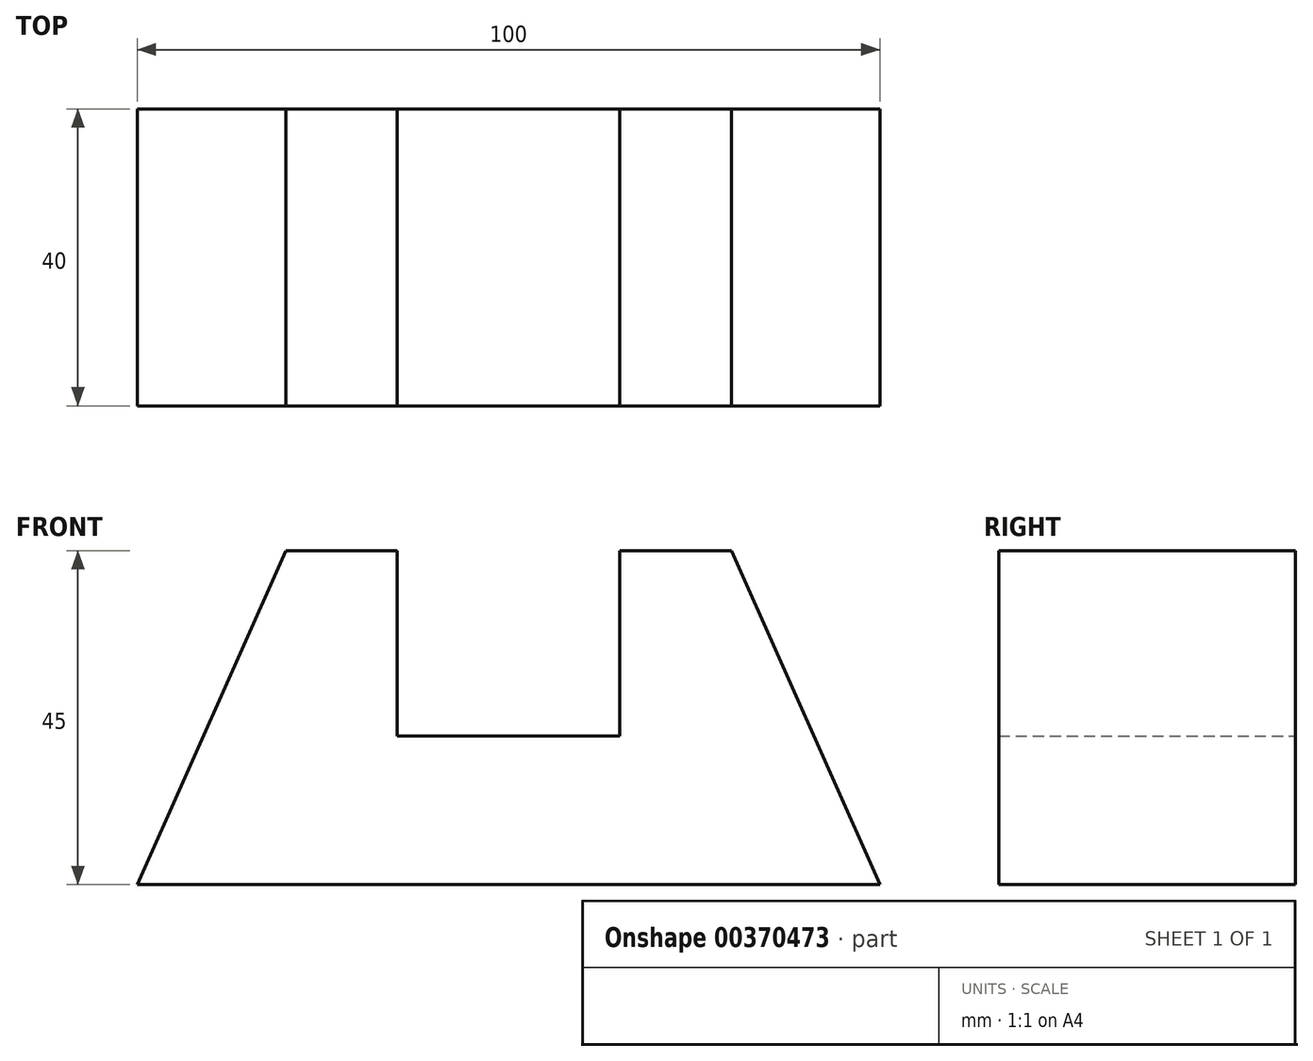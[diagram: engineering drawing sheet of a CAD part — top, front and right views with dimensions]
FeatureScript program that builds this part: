
annotation { "Feature Type Name" : "Feature", "Feature Type Description" : "" }
export const myFeature = defineFeature(function(context is Context, id is Id, definition is map)
    precondition{}
    {
        {
            var Q0;
            Q0=qCreatedBy(makeId("Front.planeOp"),FACE);
            var sketch = newSketch(context, id + "F0", { "sketchPlane" : qUnion([Q0])});
            skLineSegment(sketch, "E0", {"start": v(-50, -9.3) * mm, "end": v(50, -9.3) * mm});
            skLineSegment(sketch, "E1.MirrorCS", {"start": v(-15, 10.7) * mm, "end": v(0, 10.7) * mm});
            skLineSegment(sketch, "E2.MirrorCS", {"start": v(-15, 35.7) * mm, "end": v(-15, 10.7) * mm});
            skLineSegment(sketch, "E3.MirrorCS", {"start": v(-30, 35.7) * mm, "end": v(-15, 35.7) * mm});
            skLineSegment(sketch, "E4.MirrorCS", {"start": v(-50, -9.3) * mm, "end": v(-30, 35.7) * mm});
            skLineSegment(sketch, "E5.MirrorCS", {"start": v(15, 10.7) * mm, "end": v(0, 10.7) * mm});
            skLineSegment(sketch, "E6.MirrorCS", {"start": v(15, 35.7) * mm, "end": v(15, 10.7) * mm});
            skLineSegment(sketch, "E7.MirrorCS", {"start": v(30, 35.7) * mm, "end": v(15, 35.7) * mm});
            skLineSegment(sketch, "E8.MirrorCS", {"start": v(50, -9.3) * mm, "end": v(30, 35.7) * mm});
            skSolve(sketch);
        }
        {
            var Q0;
            Q0=makeQuery(id+"F0.imprint","IMPRINT",FACE,{"disambiguationData":[TD([[makeQuery(id+"F0.imprint","IMPRINT",EDGE,{"derivedFrom":sQuery(id+"F0.wireOp",EDGE,"E0")}),1.0]])]});
            extrude(context, id + "F1", {"entities" : qUnion([Q0]), "depth" : 40 * mm});
        }
    });
